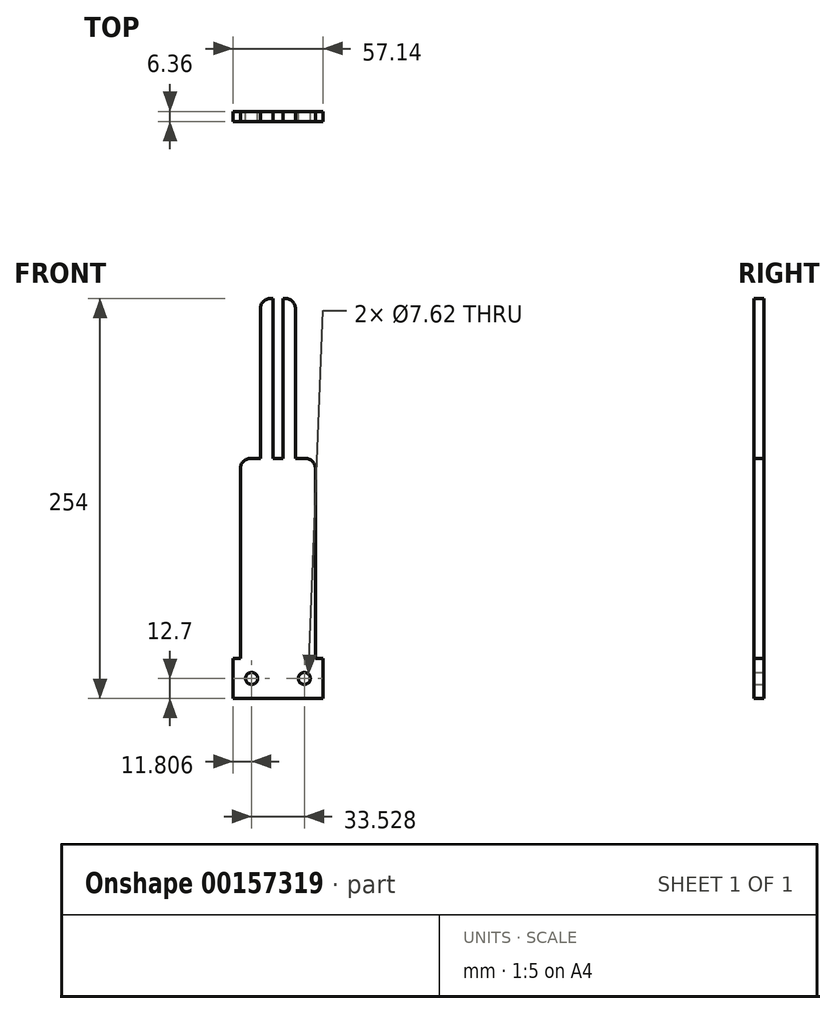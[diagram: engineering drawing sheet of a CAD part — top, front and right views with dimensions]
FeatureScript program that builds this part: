
annotation { "Feature Type Name" : "Feature", "Feature Type Description" : "" }
export const myFeature = defineFeature(function(context is Context, id is Id, definition is map)
    precondition{}
    {
        {
            var Q0;
            Q0=qCreatedBy(makeId("Front.planeOp"),FACE);
            var sketch = newSketch(context, id + "F0", { "sketchPlane" : qUnion([Q0])});
            skLineSegment(sketch, "E0.bottom", {"start": v(28.57, 12.7) * mm, "end": v(23.81, 12.7) * mm});
            skLineSegment(sketch, "E0.top", {"start": v(28.57, -12.7) * mm, "end": v(-28.58, -12.7) * mm});
            skLineSegment(sketch, "E0.left", {"start": v(28.57, 12.7) * mm, "end": v(28.57, -12.7) * mm});
            skLineSegment(sketch, "E0.right", {"start": v(-28.58, 12.7) * mm, "end": v(-28.58, -12.7) * mm});
            skPoint(sketch, "E0.middle", {"position": v(0, 0) * mm});
            skLineSegment(sketch, "E1", {"start": v(0, 0) * mm, "end": v(0, -12.7) * mm});
            skLineSegment(sketch, "E2", {"start": v(-23.81, 12.7) * mm, "end": v(-23.81, 133.35) * mm});
            skLineSegment(sketch, "E3", {"start": v(-17.46, 139.7) * mm, "end": v(-11.11, 139.7) * mm});
            skLineSegment(sketch, "E4", {"start": v(23.81, 133.35) * mm, "end": v(23.81, 12.7) * mm});
            skLineSegment(sketch, "E5", {"start": v(-4.76, 241.3) * mm, "end": v(-3.18, 241.3) * mm});
            skLineSegment(sketch, "E6", {"start": v(11.11, 234.95) * mm, "end": v(11.11, 139.7) * mm});
            skLineSegment(sketch, "E7.trimOffspring", {"start": v(-11.11, 139.7) * mm, "end": v(-11.11, 234.95) * mm});
            skLineSegment(sketch, "E8.trimOffspring", {"start": v(-3.18, 139.7) * mm, "end": v(3.17, 139.7) * mm});
            skLineSegment(sketch, "E9.trimOffspring", {"start": v(11.11, 139.7) * mm, "end": v(17.46, 139.7) * mm});
            skLineSegment(sketch, "E10.trimOffspring", {"start": v(-23.81, 12.7) * mm, "end": v(-28.58, 12.7) * mm});
            skLineSegment(sketch, "E11", {"start": v(-3.18, 139.7) * mm, "end": v(-3.18, 241.3) * mm});
            skLineSegment(sketch, "E12", {"start": v(3.17, 241.3) * mm, "end": v(3.17, 139.7) * mm});
            skLineSegment(sketch, "E13.trimOffspring", {"start": v(3.17, 241.3) * mm, "end": v(4.76, 241.3) * mm});
            skPoint(sketch, "E14.visualSharp", {"position": v(-11.11, 241.3) * mm});
            skArc(sketch, "E14.filletArc", {"start": v(-4.76, 241.3) * mm, "mid": v(-9.25, 239.44) * mm, "end": v(-11.11, 234.95) * mm});
            skPoint(sketch, "E15.visualSharp", {"position": v(11.11, 241.3) * mm});
            skArc(sketch, "E15.filletArc", {"start": v(11.11, 234.95) * mm, "mid": v(9.25, 239.44) * mm, "end": v(4.76, 241.3) * mm});
            skPoint(sketch, "E16.visualSharp", {"position": v(23.81, 139.7) * mm});
            skArc(sketch, "E16.filletArc", {"start": v(23.81, 133.35) * mm, "mid": v(21.95, 137.84) * mm, "end": v(17.46, 139.7) * mm});
            skPoint(sketch, "E17.visualSharp", {"position": v(-23.81, 139.7) * mm});
            skArc(sketch, "E17.filletArc", {"start": v(-17.46, 139.7) * mm, "mid": v(-21.95, 137.84) * mm, "end": v(-23.81, 133.35) * mm});
            skCircle(sketch, "E18", {"center": v(-16.76, 0) * mm, "radius": 3.81 * mm});
            skCircle(sketch, "E19", {"center": v(16.76, 0) * mm, "radius": 3.81 * mm});
            skLineSegment(sketch, "E20", {"start": v(0, -12.7) * mm, "end": v(-3.17, -12.7) * mm});
            skLineSegment(sketch, "E21", {"start": v(-3.17, -12.7) * mm, "end": v(-3.17, 14.57) * mm, "construction": true});
            skLineSegment(sketch, "E22.MirrorCS", {"start": v(3.17, -12.7) * mm, "end": v(3.17, 14.57) * mm, "construction": true});
            skSolve(sketch);
        }
        {
            var Q0;
            Q0=qSketchRegion(id+"F0",true);
            extrude(context, id + "F1", {"entities" : qUnion([Q0]), "endBound" : BoundingType.SYMMETRIC, "depth" : 6.35 * mm});
        }
    });
